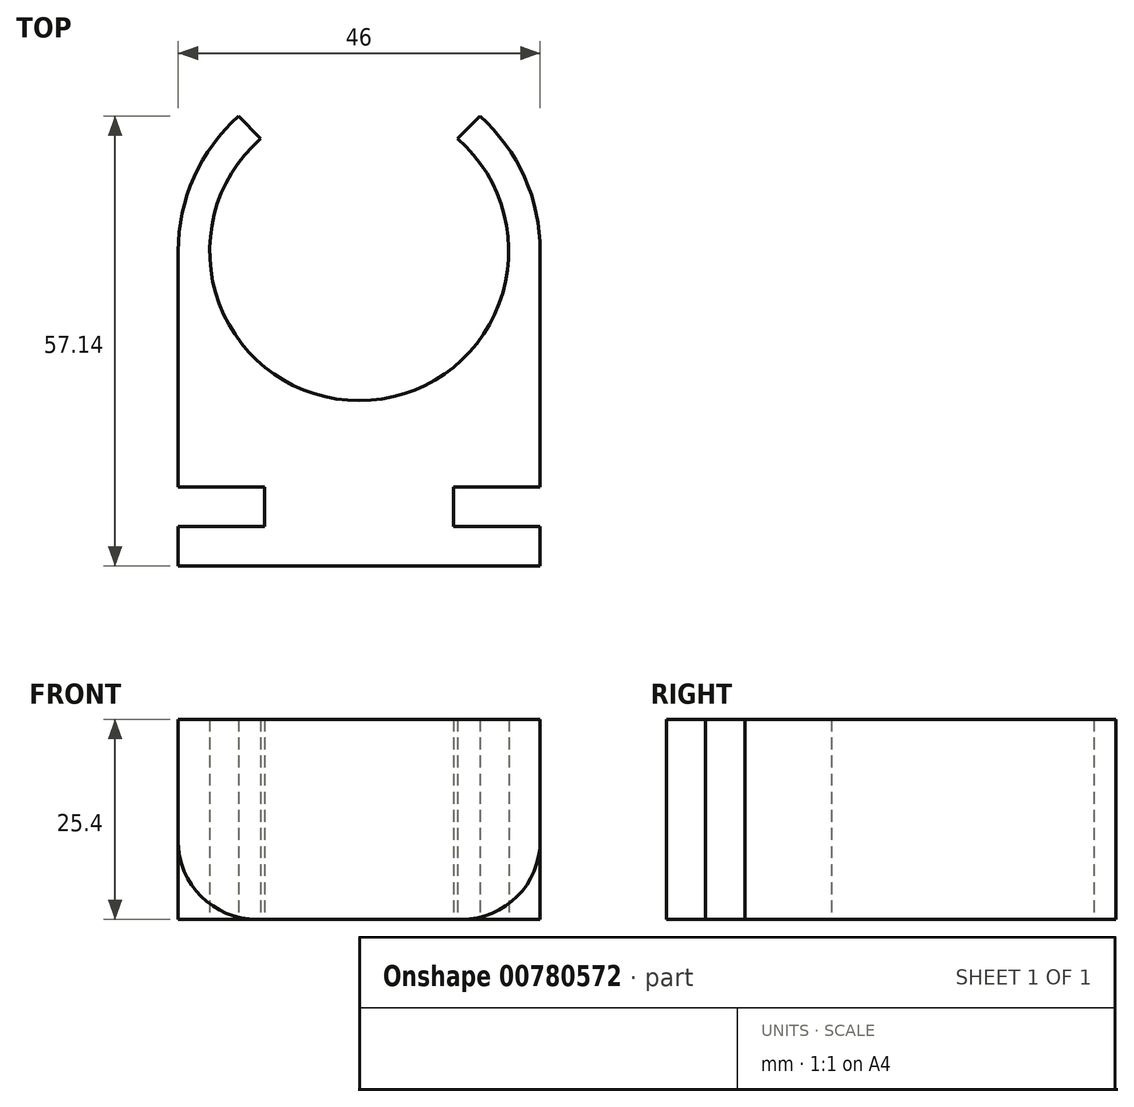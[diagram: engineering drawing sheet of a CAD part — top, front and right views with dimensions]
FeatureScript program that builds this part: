
annotation { "Feature Type Name" : "Feature", "Feature Type Description" : "" }
export const myFeature = defineFeature(function(context is Context, id is Id, definition is map)
    precondition{}
    {
        {
            var Q0;
            Q0=qCreatedBy(makeId("Top.planeOp"),FACE);
            var sketch = newSketch(context, id + "F0", { "sketchPlane" : qUnion([Q0])});
            skArc(sketch, "E0", {"start": v(-12.5, 14.3) * mm, "mid": v(0, -19) * mm, "end": v(12.5, 14.3) * mm});
            skArc(sketch, "E1", {"start": v(-15.33, 17.14) * mm, "mid": v(-21, 9.39) * mm, "end": v(-23, 0) * mm});
            skLineSegment(sketch, "E2", {"start": v(-15.33, 17.14) * mm, "end": v(-12.5, 14.3) * mm});
            skLineSegment(sketch, "E3", {"start": v(12.5, 14.3) * mm, "end": v(15.33, 17.14) * mm});
            skPoint(sketch, "E4.orphan", {"position": v(0, 1.8) * mm});
            skLineSegment(sketch, "E5", {"start": v(-23, 0) * mm, "end": v(-23, -30) * mm});
            skLineSegment(sketch, "E6", {"start": v(-23, -40) * mm, "end": v(23, -40) * mm});
            skLineSegment(sketch, "E7", {"start": v(23, -40) * mm, "end": v(23, -35) * mm});
            skArc(sketch, "E8.trimOffspring", {"start": v(23, 0) * mm, "mid": v(21, 9.39) * mm, "end": v(15.33, 17.14) * mm});
            skLineSegment(sketch, "E9.bottom", {"start": v(-23, -35) * mm, "end": v(-12, -35) * mm});
            skLineSegment(sketch, "E9.top", {"start": v(-23, -30) * mm, "end": v(-12, -30) * mm});
            skLineSegment(sketch, "E9.right", {"start": v(-12, -35) * mm, "end": v(-12, -30) * mm});
            skLineSegment(sketch, "E10.MirrorCS", {"start": v(23, -35) * mm, "end": v(12, -35) * mm});
            skLineSegment(sketch, "E11.MirrorCS", {"start": v(23, -30) * mm, "end": v(12, -30) * mm});
            skLineSegment(sketch, "E12.MirrorCS", {"start": v(12, -35) * mm, "end": v(12, -30) * mm});
            skPoint(sketch, "E13.orphan", {"position": v(-26.68, -35) * mm});
            skPoint(sketch, "E14.orphan", {"position": v(-26.68, -30) * mm});
            skLineSegment(sketch, "E15.trimOffspring", {"start": v(-23, -35) * mm, "end": v(-23, -40) * mm});
            skPoint(sketch, "E16.orphan", {"position": v(26.68, -30) * mm});
            skPoint(sketch, "E17.orphan", {"position": v(26.68, -35) * mm});
            skLineSegment(sketch, "E18.trimOffspring", {"start": v(23, -30) * mm, "end": v(23, 0) * mm});
            skSolve(sketch);
        }
        {
            var Q0;
            Q0=makeQuery(id+"F0.imprint","IMPRINT",FACE,{"disambiguationData":[TD([[makeQuery(id+"F0.imprint","IMPRINT",EDGE,{"derivedFrom":sQuery(id+"F0.wireOp",EDGE,"E0")}),-1.0]])]});
            extrude(context, id + "F1", {"entities" : qUnion([Q0]), "depth" : 25.4 * mm, "offsetDistance" : 25.4 * mm});
        }
        {
            var Q0;
            Q0=makeQuery(id+"F1.opExtrude","CAP_EDGE",EDGE,{"disambiguationData":[OSD([sQuery(id+"F0.wireOp",EDGE,"E7")])],"isStart":true});
            fillet(context, id + "F2", {"entities" : qUnion([Q0]), "radius" : 10 * mm, "allowEdgeOverflow" : false});
        }
        {
            var Q0;
            Q0=makeQuery(id+"F1.opExtrude","CAP_EDGE",EDGE,{"disambiguationData":[OSD([sQuery(id+"F0.wireOp",EDGE,"E15.trimOffspring")])],"isStart":true});
            fillet(context, id + "F3", {"entities" : qUnion([Q0]), "radius" : 10 * mm, "tangentPropagation" : true, "allowEdgeOverflow" : false});
        }
    });
